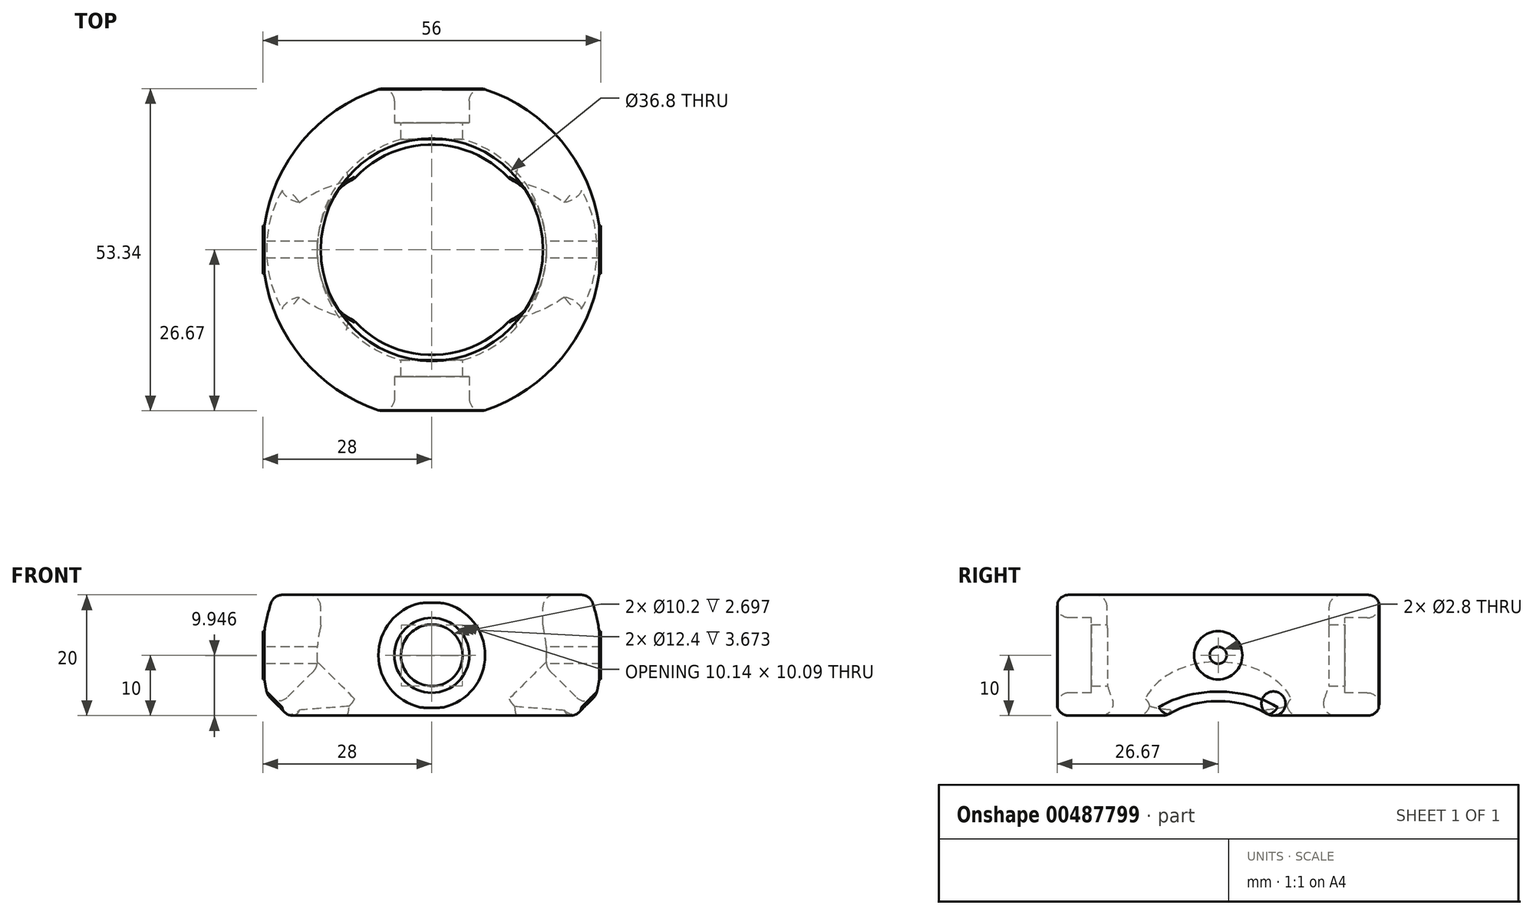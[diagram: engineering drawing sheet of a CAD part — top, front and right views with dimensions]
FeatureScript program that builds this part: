
annotation { "Feature Type Name" : "Feature", "Feature Type Description" : "" }
export const myFeature = defineFeature(function(context is Context, id is Id, definition is map)
    precondition{}
    {
        {
            var Q0;
            Q0=qCreatedBy(makeId("Front.planeOp"),FACE);
            var sketch = newSketch(context, id + "F0", { "sketchPlane" : qUnion([Q0])});
            skCircle(sketch, "E0", {"center": v(0, 0) * mm, "radius": 19 * mm});
            skCircle(sketch, "E1", {"center": v(0, 0) * mm, "radius": 28 * mm});
            skLineSegment(sketch, "E2.bottom", {"start": v(0, 0) * mm, "end": v(18.4, 0) * mm});
            skLineSegment(sketch, "E2.top", {"start": v(0, 10) * mm, "end": v(18.4, 10) * mm});
            skLineSegment(sketch, "E2.left", {"start": v(0, 0) * mm, "end": v(0, 10) * mm});
            skLineSegment(sketch, "E2.right", {"start": v(18.4, 0) * mm, "end": v(18.4, 10) * mm});
            skLineSegment(sketch, "E3.bottom", {"start": v(0, 10) * mm, "end": v(40, 10) * mm});
            skLineSegment(sketch, "E3.top", {"start": v(0, -10) * mm, "end": v(40, -10) * mm});
            skLineSegment(sketch, "E3.left", {"start": v(0, 10) * mm, "end": v(0, -10) * mm});
            skLineSegment(sketch, "E3.right", {"start": v(40, 10) * mm, "end": v(40, -10) * mm});
            skSolve(sketch);
        }
        {
            var Q0;
            {var subQ1=sQuery(id+"F0.wireOp",EDGE,"E2.right");var subQ7=sQuery(id+"F0.wireOp",EDGE,"E0");var subQ8=makeQuery(id+"F0.imprint","INTERSECT",VERTEX,{"derivedFrom":[subQ7,subQ1]});Q0=makeQuery(id+"F0.imprint","IMPRINT",FACE,{"disambiguationData":[TD([[makeQuery(id+"F0.imprint","IMPRINT",EDGE,{"disambiguationData":[TD([[subQ8,1.0]])],"derivedFrom":subQ7}),-1.0]])]});}
            var Q1;
            Q1=sQuery(id+"F0.wireOp",EDGE,"E3.left");
            revolve(context, id + "F1", {"entities" : qUnion([Q0]), "axis" : qUnion([Q1]), "revolveType" : RevolveType.FULL});
        }
        {
            var Q0;
            Q0=qCreatedBy(makeId("Front.planeOp"),FACE);
            var sketch = newSketch(context, id + "F2", { "sketchPlane" : qUnion([Q0])});
            skCircle(sketch, "E4", {"center": v(0, 0) * mm, "radius": 5.1 * mm});
            skCircle(sketch, "E5", {"center": v(0, 0) * mm, "radius": 6.2 * mm});
            skSolve(sketch);
        }
        {
            var Q0;
            Q0=makeQuery(id+"F2.imprint","IMPRINT",FACE,{"disambiguationData":[TD([[makeQuery(id+"F2.imprint","IMPRINT",EDGE,{"derivedFrom":sQuery(id+"F2.wireOp",EDGE,"E4")}),1.0]])]});
            var Q1;
            Q1=makeQuery(id+"F2.imprint","IMPRINT",FACE,{"disambiguationData":[TD([[makeQuery(id+"F2.imprint","IMPRINT",EDGE,{"derivedFrom":sQuery(id+"F2.wireOp",EDGE,"E4")}),-1.0]])]});
            extrude(context, id + "F3", {"entities" : qUnion([Q0, Q1]), "operationType" : NewBodyOperationType.REMOVE, "endBound" : BoundingType.SYMMETRIC, "oppositeDirection" : true, "depth" : 120 * mm});
        }
        {
            var Q0;
            Q0=makeQuery(id+"F2.imprint","IMPRINT",FACE,{"disambiguationData":[TD([[makeQuery(id+"F2.imprint","IMPRINT",EDGE,{"derivedFrom":sQuery(id+"F2.wireOp",EDGE,"E4")}),-1.0]])]});
            extrude(context, id + "F4", {"entities" : qUnion([Q0]), "operationType" : NewBodyOperationType.ADD, "endBound" : BoundingType.SYMMETRIC, "depth" : (36 + 6) * mm});
        }
        {
            var Q0;
            Q0=qCreatedBy(makeId("Right.planeOp"),FACE);
            var sketch = newSketch(context, id + "F5", { "sketchPlane" : qUnion([Q0])});
            skCircle(sketch, "E6", {"center": v(0, 0) * mm, "radius": 4 * mm});
            skCircle(sketch, "E7", {"center": v(0, 0) * mm, "radius": 1.4 * mm});
            skSolve(sketch);
        }
        {
            var Q0;
            Q0=makeQuery(id+"F5.imprint","IMPRINT",FACE,{"disambiguationData":[TD([[makeQuery(id+"F5.imprint","IMPRINT",EDGE,{"derivedFrom":sQuery(id+"F5.wireOp",EDGE,"E6")}),1.0]])]});
            extrude(context, id + "F6", {"entities" : qUnion([Q0]), "operationType" : NewBodyOperationType.ADD, "endBound" : BoundingType.SYMMETRIC, "depth" : 56 * mm});
        }
        {
            var Q0;
            Q0=makeQuery(id+"F5.imprint","IMPRINT",FACE,{"disambiguationData":[TD([[makeQuery(id+"F5.imprint","IMPRINT",EDGE,{"derivedFrom":sQuery(id+"F5.wireOp",EDGE,"E7")}),1.0]])]});
            extrude(context, id + "F7", {"entities" : qUnion([Q0]), "operationType" : NewBodyOperationType.REMOVE, "endBound" : BoundingType.SYMMETRIC, "oppositeDirection" : true, "depth" : 100 * mm});
        }
        {
            var Q0;
            {var subQ1=sQuery(id+"F0.wireOp",EDGE,"E2.bottom");Q0=makeQuery(id+"F0.imprint","IMPRINT",FACE,{"disambiguationData":[TD([[makeQuery(id+"F0.imprint","IMPRINT",EDGE,{"derivedFrom":subQ1}),-1.0]])]});}
            var Q1;
            {var subQ6=sQuery(id+"F0.wireOp",EDGE,"E2.bottom");Q1=makeQuery(id+"F0.imprint","IMPRINT",FACE,{"disambiguationData":[TD([[makeQuery(id+"F0.imprint","IMPRINT",EDGE,{"derivedFrom":subQ6}),1.0]])]});}
            var Q2;
            {var subQ0=sQuery(id+"F0.wireOp",EDGE,"E3.bottom");var subQ1=sQuery(id+"F0.wireOp",EDGE,"E0");var subQ2=makeQuery(id+"F0.imprint","INTERSECT",VERTEX,{"derivedFrom":[subQ1,subQ0]});Q2=makeQuery(id+"F0.imprint","IMPRINT",FACE,{"disambiguationData":[TD([[makeQuery(id+"F0.imprint","IMPRINT",EDGE,{"disambiguationData":[TD([[subQ2,1.0]])],"derivedFrom":subQ1}),-1.0]])]});}
            var Q3;
            Q3=sQuery(id+"F0.wireOp",EDGE,"E3.left");
            revolve(context, id + "F8", {"operationType" : NewBodyOperationType.REMOVE, "entities" : qUnion([Q0, Q1, Q2]), "axis" : qUnion([Q3]), "revolveType" : RevolveType.FULL, "oppositeDirection" : true});
        }
        {
            var Q0;
            Q0=qCreatedBy(makeId("Front.planeOp"),FACE);
            var sketch = newSketch(context, id + "F9", { "sketchPlane" : qUnion([Q0])});
            skLineSegment(sketch, "E8.bottom", {"start": v(0, 0) * mm, "end": v(60, 0) * mm});
            skLineSegment(sketch, "E8.top", {"start": v(0, -60) * mm, "end": v(60, -60) * mm});
            skLineSegment(sketch, "E8.left", {"start": v(0, 0) * mm, "end": v(0, -60) * mm});
            skLineSegment(sketch, "E8.right", {"start": v(60, 0) * mm, "end": v(60, -60) * mm});
            skLineSegment(sketch, "E9", {"start": v(0, 0) * mm, "end": v(60, -60) * mm});
            skLineSegment(sketch, "E10", {"start": v(60, 0) * mm, "end": v(0, -60) * mm});
            skLineSegment(sketch, "E11", {"start": v(38.49, -21.51) * mm, "end": v(16.97, 0) * mm});
            skLineSegment(sketch, "E12.MirrorCS", {"start": v(0, 0) * mm, "end": v(-60, 0) * mm});
            skLineSegment(sketch, "E13.MirrorCS", {"start": v(0, 0) * mm, "end": v(-60, -60) * mm});
            skLineSegment(sketch, "E14.MirrorCS", {"start": v(-60, 0) * mm, "end": v(0, -60) * mm});
            skLineSegment(sketch, "E15.MirrorCS", {"start": v(-38.49, -21.51) * mm, "end": v(-16.97, 0) * mm});
            skSolve(sketch);
        }
        {
            var Q0;
            {var subQ3=sQuery(id+"F9.wireOp",EDGE,"E11");Q0=makeQuery(id+"F9.imprint","IMPRINT",FACE,{"disambiguationData":[TD([[makeQuery(id+"F9.imprint","IMPRINT",EDGE,{"derivedFrom":subQ3}),1.0]])]});}
            var Q1;
            Q1=sQuery(id+"F9.wireOp",EDGE,"E9");
            revolve(context, id + "F10", {"operationType" : NewBodyOperationType.REMOVE, "entities" : qUnion([Q0]), "axis" : qUnion([Q1]), "revolveType" : RevolveType.FULL, "oppositeDirection" : true});
        }
        {
            var Q0;
            {var subQ3=sQuery(id+"F9.wireOp",EDGE,"E15.MirrorCS");Q0=makeQuery(id+"F9.imprint","IMPRINT",FACE,{"disambiguationData":[TD([[makeQuery(id+"F9.imprint","IMPRINT",EDGE,{"derivedFrom":subQ3}),-1.0]])]});}
            var Q1;
            Q1=sQuery(id+"F9.wireOp",EDGE,"E13.MirrorCS");
            revolve(context, id + "F11", {"operationType" : NewBodyOperationType.REMOVE, "entities" : qUnion([Q0]), "axis" : qUnion([Q1]), "revolveType" : RevolveType.FULL, "oppositeDirection" : true});
        }
        {
            var Q0;
            Q0=makeQuery(id+"F11.boolean.opBoolean","COPY",FACE,{"derivedFrom":makeQuery(id+"F11.opRevolve","SWEPT_FACE",FACE,{"disambiguationData":[OSD([sQuery(id+"F9.wireOp",EDGE,"E15.MirrorCS")])]})});
            var Q1;
            Q1=makeQuery(id+"F10.boolean.opBoolean","COPY",FACE,{"derivedFrom":makeQuery(id+"F10.opRevolve","SWEPT_FACE",FACE,{"disambiguationData":[OSD([sQuery(id+"F9.wireOp",EDGE,"E11")])]})});
            var Q2;
            Q2=makeQuery(id+"F11.boolean.opBoolean","SPLIT",FACE,{"disambiguationData":[OD(0.0)],"derivedFrom":makeQuery(id+"F1.opRevolve","SWEPT_FACE",FACE,{"disambiguationData":[OSD([sQuery(id+"F0.wireOp",EDGE,"E3.top")])]})});
            var Q3;
            Q3=makeQuery(id+"F11.boolean.opBoolean","SPLIT",FACE,{"disambiguationData":[OD(1.0)],"derivedFrom":makeQuery(id+"F1.opRevolve","SWEPT_FACE",FACE,{"disambiguationData":[OSD([sQuery(id+"F0.wireOp",EDGE,"E3.top")])]})});
            var Q4;
            Q4=makeQuery(id+"F1.opRevolve","SWEPT_FACE",FACE,{"disambiguationData":[OSD([sQuery(id+"F0.wireOp",EDGE,"E3.bottom")])]});
            var Q5;
            {var subQ0=sQuery(id+"F0.wireOp",EDGE,"E2.right");var subQ1=sQuery(id+"F0.wireOp",EDGE,"E0");var subQ2=makeQuery(id+"F1.opRevolve","SWEPT_EDGE",EDGE,{"disambiguationData":[OSD([subQ1,subQ0])]});Q5=makeQuery(id+"F8.boolean.opBoolean","MERGE",EDGE,{"derivedFrom":[makeQuery(id+"F3.boolean.opBoolean","SPLIT",EDGE,{"disambiguationData":[OD(0.0)],"derivedFrom":subQ2}),makeQuery(id+"F3.boolean.opBoolean","SPLIT",EDGE,{"disambiguationData":[OD(1.0)],"derivedFrom":subQ2}),makeQuery(id+"F8.opRevolve","SWEPT_EDGE",EDGE,{"disambiguationData":[OSD([subQ1,subQ0])]})]});}
            var Q6;
            Q6=makeQuery(id+"F3.boolean.opBoolean","INTERSECT",EDGE,{"disambiguationData":[OD(0.0)],"derivedFrom":[makeQuery(id+"F1.opRevolve","SWEPT_FACE",FACE,{"disambiguationData":[OSD([sQuery(id+"F0.wireOp",EDGE,"E1")])]}),makeQuery(id+"F3.opExtrude","SWEPT_FACE",FACE,{"disambiguationData":[OSD([sQuery(id+"F2.wireOp",EDGE,"E5")])]})]});
            var Q7;
            Q7=makeQuery(id+"F3.boolean.opBoolean","INTERSECT",EDGE,{"disambiguationData":[OD(1.0)],"derivedFrom":[makeQuery(id+"F1.opRevolve","SWEPT_FACE",FACE,{"disambiguationData":[OSD([sQuery(id+"F0.wireOp",EDGE,"E1")])]}),makeQuery(id+"F3.opExtrude","SWEPT_FACE",FACE,{"disambiguationData":[OSD([sQuery(id+"F2.wireOp",EDGE,"E5")])]})]});
            fillet(context, id + "F12", {"entities" : qUnion([Q0, Q1, Q2, Q3, Q4, Q5, Q6, Q7]), "radius" : 2 * mm, "tangentPropagation" : true, "allowEdgeOverflow" : false});
        }
    });
